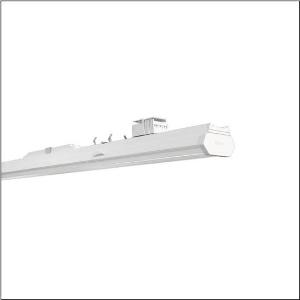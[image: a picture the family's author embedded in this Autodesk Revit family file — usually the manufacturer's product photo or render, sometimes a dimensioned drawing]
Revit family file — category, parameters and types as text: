
# Revit family: licross_r__21_protected_mo_52td1bcn485g_f119
name_source: partatom
category: Lighting Fixtures
units: mm (PartAtom-declared; Revit-internal decimal feet)

## family parameters
Cut with Voids When Loaded = No
Host = Face
Light Source = No
Part Type = Normal
Room Calculation Point = No
Round Connector Dimension = Use Diameter
Shared = No

## types (1)
- --- (1 x LED, 8570 lm, 50.4 W, 4000K)
    Apparent Load = 50 VA
    CIE Flux Codes = 54 82 95 97 100
    Color Rendering = 80
    Color Temperature = 4000K
    Default Elevation = 1800 mm
    Description = Licross® 21 Protected MO, luminaire insert, of sheet steel, galvanised, coil coated, white, length: 1.500mm, width: 90mm, height: 103mm, LED rated luminous flux: 8.570lm, light colour: 840, control gear: ON/OFF Multilumen, CLOi, control gear: ECG Multilumen, with plug, 3-pole, with phase selection, mains connection: 220..240V, AC, 50/60Hz, start of lifetime: 50W, end of service life: 61W, halogen-free wiring, primary optical cover: cover, of PMMA, light emission: direct distribution, primary light characteristic: symmetric, protection rating (complete): IP54, insulation class (complete): insulation class I (protective earthing), certification: CE, ENEC, VDE, UKCA, protection symbol: D if used in an environment with non-conductive dust loads with corresponding accessories, impact resistance: IK06, permissible ambient temperature for indoor applications: -35..+45°C, corresponds to IFS (International Featured Standards) requirements for safety and quality in the food industry, reducing of maximum allowable ambient temperature of 5°C with ceiling mounting, LABS conformity tested according to VDMA 24364:2018-05, packaging unit: 1 piece
    Height = 92 mm
    Lamp = 1 x LED
    Lamp Light Flux = 8570 lm
    Lamp Power = 50.4 W
    Lamp count = 1
    Length = 1500 mm
    Luminous efficacy = 170 lm/W
    Manufacturer = Siteco
    ModVariant = No
    Model = 52TD1BCN485G
    Mounting Place = Ceiling
    Mounting Type = Pendant
    Number of Poles = 1
    OnlyDefault = Yes
    Power Factor = 1
    Product Name = Licross® 21 Protected MO
    Product group = luminaire insert
    ProductGroupID = 901
    Protection Class = Protection class I
    Protection Degree = IP 54
    RLX_Detail_Level = 1
    RLX_Emergency_Light_Flux = 0 lm
    RLX_Emergency_Type = 0
    RLX_Emergency_Type_DB = No
    RlxData = <blob elided: 22141 chars, md5=e370d949>
    Socket = socket
    Standby Power = 0 W
    System Light Flux = 8570 lm
    System Power = 50 W
    Type Comments = factory setting: luminous flux: 100 % | (A | C | E) | 117 mA
    Type Image = l_1256148.jpg
    URL = http://relux.com
    VarID = @adj_080365
    Voltage = 0 V
    Weight = 0.00 kg
    Width = 88 mm

## geometry (parser evidence)
native form markers: Blend x4, Sweep x12
no freeform markers — native parametric forms only
